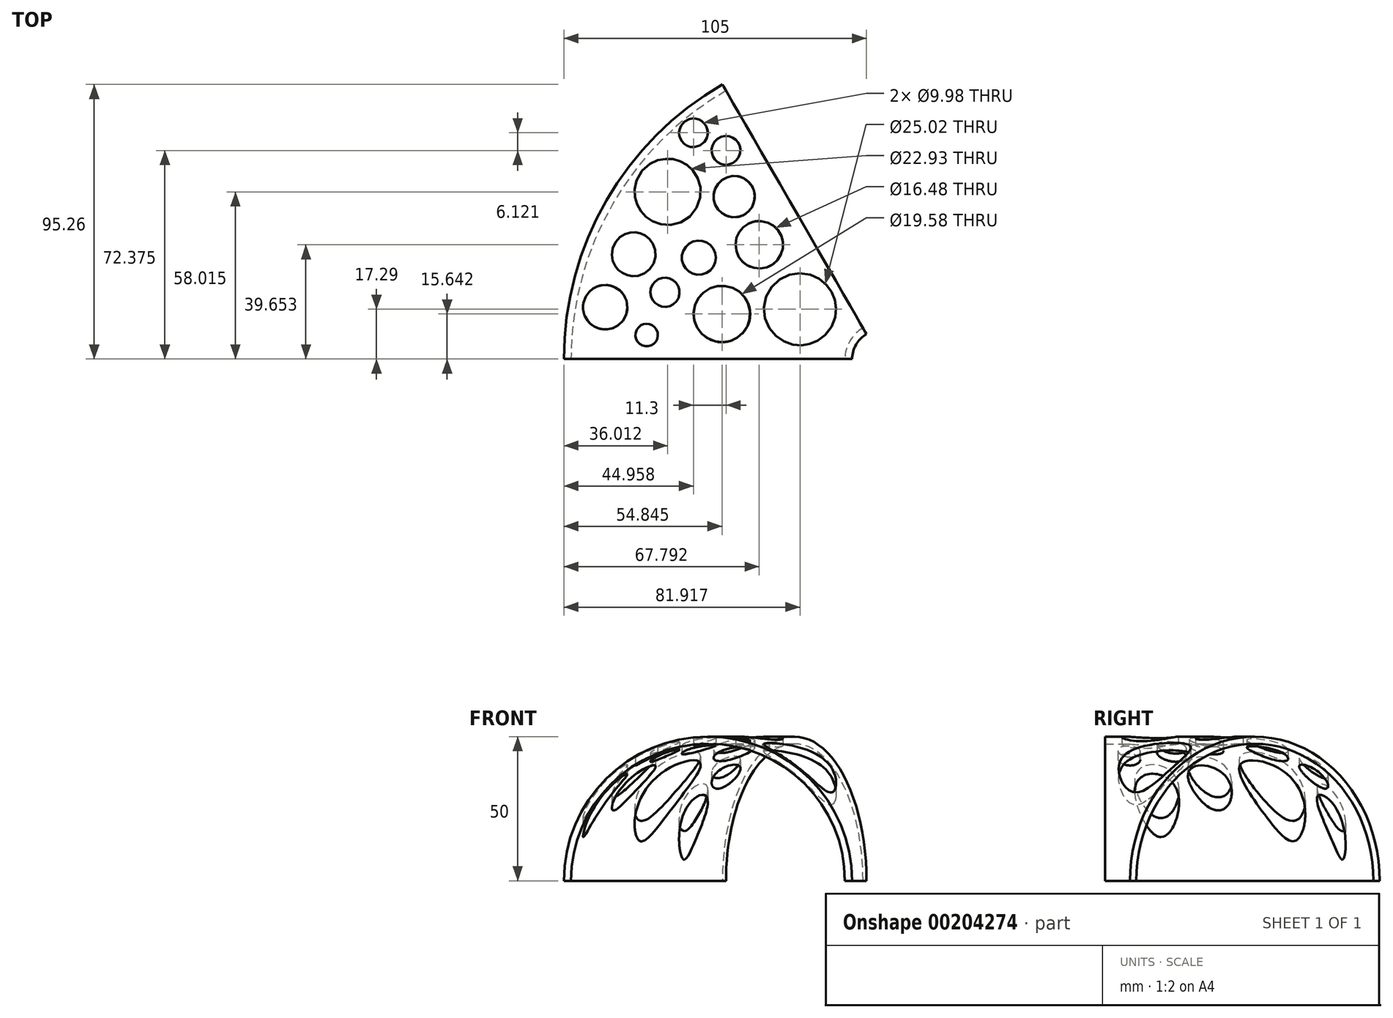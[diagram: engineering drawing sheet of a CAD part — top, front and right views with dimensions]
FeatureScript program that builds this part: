
annotation { "Feature Type Name" : "Feature", "Feature Type Description" : "" }
export const myFeature = defineFeature(function(context is Context, id is Id, definition is map)
    precondition{}
    {
        {
            var Q0;
            Q0=qCreatedBy(makeId("Front.planeOp"),FACE);
            var sketch = newSketch(context, id + "F0", { "sketchPlane" : qUnion([Q0])});
            skArc(sketch, "E0", {"start": v(47.5, -15.52) * mm, "mid": v(0, 31.98) * mm, "end": v(-47.5, -15.52) * mm});
            skArc(sketch, "E1", {"start": v(50, -15.52) * mm, "mid": v(0, 34.48) * mm, "end": v(-50, -15.52) * mm});
            skLineSegment(sketch, "E2", {"start": v(-50, -15.52) * mm, "end": v(-47.5, -15.52) * mm});
            skLineSegment(sketch, "E3.trimOffspring", {"start": v(47.5, -15.52) * mm, "end": v(50, -15.52) * mm});
            skLineSegment(sketch, "E4", {"start": v(60, -15.52) * mm, "end": v(60, 3.24) * mm, "construction": true});
            skSolve(sketch);
        }
        {
            var Q0;
            Q0 = qSketchRegion(id + "F0", true);
            var Q1;
            Q1=sQuery(id+"F0.wireOp",EDGE,"E4");
            revolve(context, id + "F1", {"entities" : qUnion([Q0]), "axis" : qUnion([Q1]), "revolveType" : RevolveType.ONE_DIRECTION, "oppositeDirection" : true, "angle" : 60 * degree});
        }
        {
            var Q0;
            Q0=qCreatedBy(makeId("Top.planeOp"),FACE);
            var sketch = newSketch(context, id + "F2", { "sketchPlane" : qUnion([Q0])});
            skCircle(sketch, "E5", {"center": v(-5.04, 78.5) * mm, "radius": 4.99 * mm});
            skCircle(sketch, "E6", {"center": v(-13.99, 58.01) * mm, "radius": 11.47 * mm});
            skCircle(sketch, "E7", {"center": v(-25.76, 36.36) * mm, "radius": 7.6 * mm});
            skCircle(sketch, "E8", {"center": v(9.08, 56.37) * mm, "radius": 7.15 * mm});
            skCircle(sketch, "E9", {"center": v(17.8, 39.65) * mm, "radius": 8.24 * mm});
            skCircle(sketch, "E10", {"center": v(4.84, 15.64) * mm, "radius": 9.8 * mm});
            skCircle(sketch, "E11", {"center": v(-3.16, 35.18) * mm, "radius": 5.91 * mm});
            skCircle(sketch, "E12", {"center": v(-21.29, 8.34) * mm, "radius": 3.9 * mm});
            skCircle(sketch, "E13", {"center": v(-35.65, 18) * mm, "radius": 7.7 * mm});
            skCircle(sketch, "E14", {"center": v(-14.93, 23.17) * mm, "radius": 5.07 * mm});
            skCircle(sketch, "E15", {"center": v(31.92, 17.29) * mm, "radius": 12.5 * mm});
            skCircle(sketch, "E16", {"center": v(6.26, 72.37) * mm, "radius": 4.99 * mm});
            skSolve(sketch);
        }
        {
            var Q0;
            Q0 = qSketchRegion(id + "F2", true);
            var Q1;
            Q1=sQuery(id+"F2.wireOp",EDGE,"E16");
            extrude(context, id + "F3", {"entities" : qUnion([Q0]), "operationType" : NewBodyOperationType.REMOVE, "surfaceEntities" : qUnion([Q1]), "depth" : 40 * mm, "hasSecondDirection" : true, "secondDirectionOppositeDirection" : true, "secondDirectionDepth" : 25 * mm});
        }
    });
